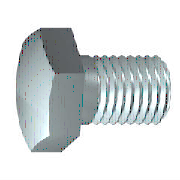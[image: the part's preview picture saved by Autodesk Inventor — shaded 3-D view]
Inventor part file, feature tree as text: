
AUTODESK INVENTOR PART (.ipt)
format: ipt  version: 2023 (Build 270158000, 158)  size: 213,504 bytes
history: native  units: mm (DEFAULTED — no unit token found)
features: other x3, sketch x2, extrude x1, fillet x1
ambient origin geometry x8: Origin, YZ Plane, XZ Plane, XY Plane, X Axis, Y Axis, Z Axis, Center Point
bodies: Solid1 (feature_tree)
feature tree (7):
  extrude  "Extrusion2"  TaperAngle=45.0deg  [1 undecoded]
  other  "MSC_A1"
  other  "MSC_PF1"
  other  "MSC_PT1"
  fillet  "Fillet1"  [1 undecoded]
  sketch  "Schizzo3"
  sketch  "Sketch5"  dims[d3=30.0deg d5=45.0deg d8=90.0deg d9=60.0deg d13=0.0mm d14=30.0deg d16=90.0deg d18=0.0mm d22=0.0mm d23=0.0mm d25=0.0mm d26=0.0mm d27=18.0mm d28=2.0mm d29=0.0mm d30=0.6mm d31=0.0mm]
note: 2 required parameter values undecoded (feature->parameter linkage not recoverable at this tier; creation-order binding heuristic only, values carry confidence <= 0.55)
